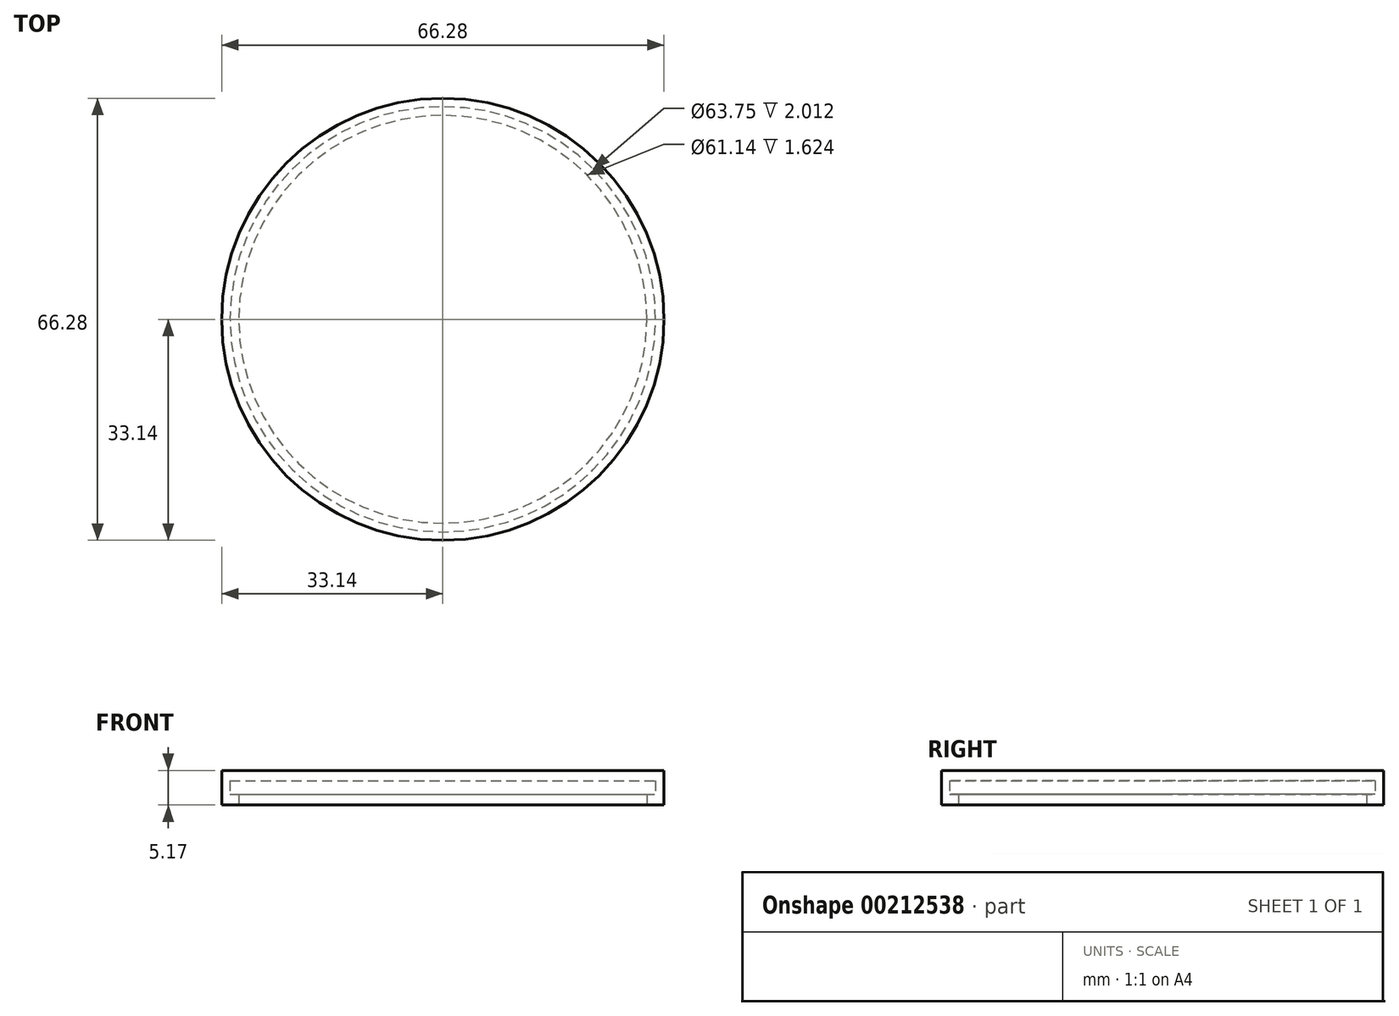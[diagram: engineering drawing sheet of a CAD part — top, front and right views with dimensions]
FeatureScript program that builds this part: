
annotation { "Feature Type Name" : "Feature", "Feature Type Description" : "" }
export const myFeature = defineFeature(function(context is Context, id is Id, definition is map)
    precondition{}
    {
        {
            var Q0;
            Q0=qCreatedBy(makeId("Right.planeOp"),FACE);
            var sketch = newSketch(context, id + "F0", { "sketchPlane" : qUnion([Q0])});
            skLineSegment(sketch, "E0", {"start": v(33.14, 0) * mm, "end": v(33.14, 5.17) * mm});
            skLineSegment(sketch, "E1", {"start": v(33.14, 5.17) * mm, "end": v(0, 5.17) * mm});
            skLineSegment(sketch, "E2", {"start": v(33.14, 0) * mm, "end": v(30.57, 0) * mm});
            skLineSegment(sketch, "E3", {"start": v(30.57, 0) * mm, "end": v(30.57, 1.62) * mm});
            skLineSegment(sketch, "E4", {"start": v(30.57, 1.62) * mm, "end": v(31.87, 1.62) * mm});
            skLineSegment(sketch, "E5", {"start": v(31.87, 1.62) * mm, "end": v(31.87, 3.64) * mm});
            skLineSegment(sketch, "E6", {"start": v(31.87, 3.64) * mm, "end": v(0, 3.64) * mm});
            skLineSegment(sketch, "E7", {"start": v(0, 0) * mm, "end": v(0, 15.2) * mm});
            skSolve(sketch);
        }
        {
            var Q0;
            Q0 = qSketchRegion(id + "F0", true);
            var Q1;
            Q1=sQuery(id+"F0.wireOp",EDGE,"E7");
            revolve(context, id + "F1", {"entities" : qUnion([Q0]), "axis" : qUnion([Q1]), "revolveType" : RevolveType.FULL});
        }
    });
